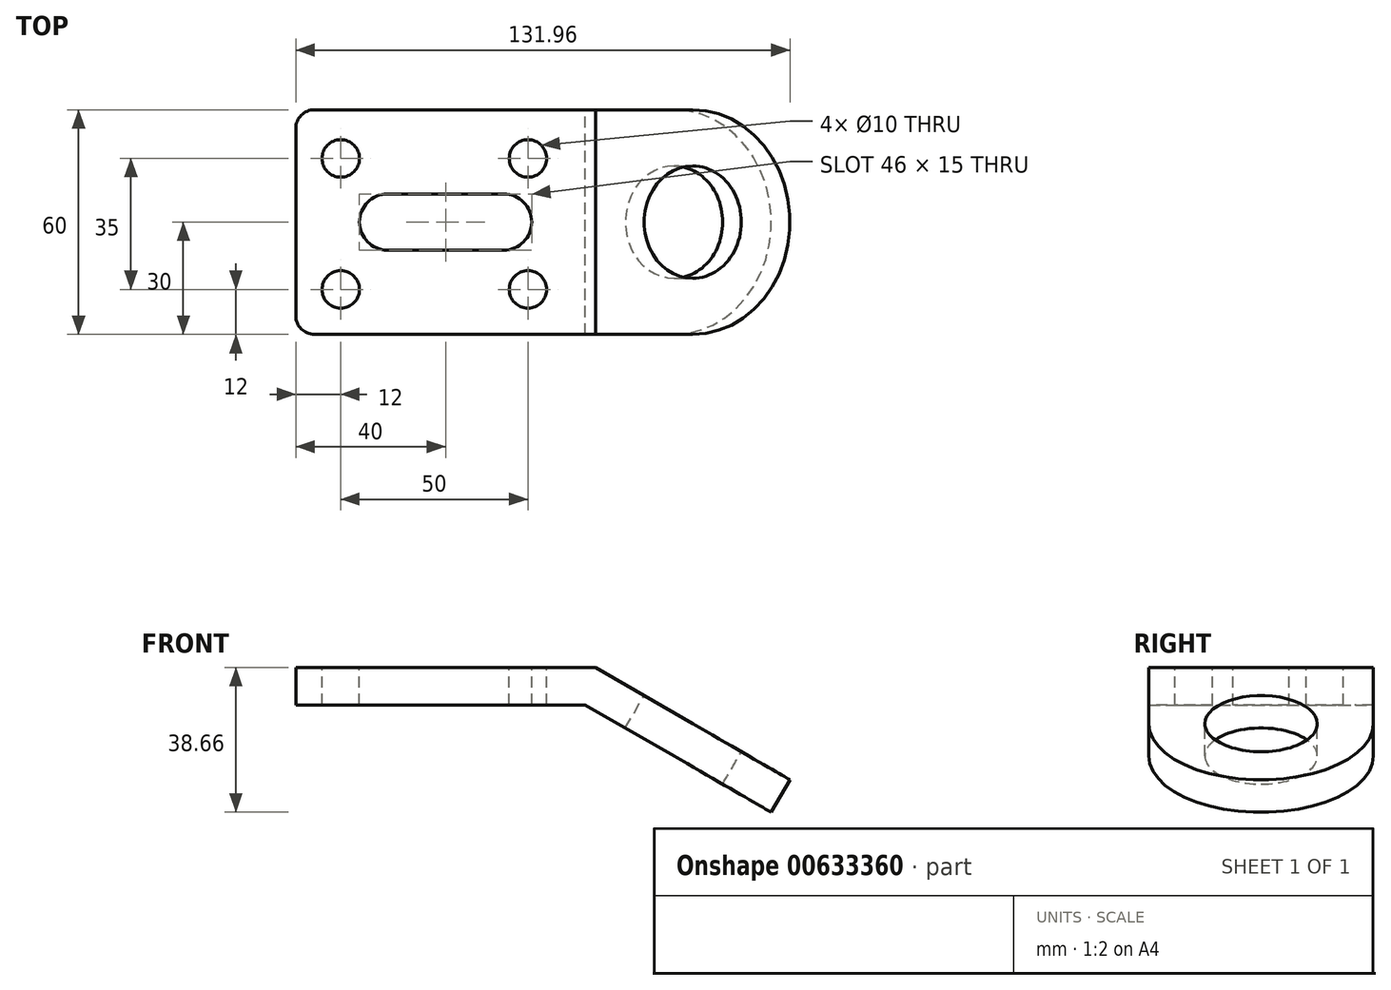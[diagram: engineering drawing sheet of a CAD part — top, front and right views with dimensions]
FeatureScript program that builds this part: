
annotation { "Feature Type Name" : "Feature", "Feature Type Description" : "" }
export const myFeature = defineFeature(function(context is Context, id is Id, definition is map)
    precondition{}
    {
        {
            var Q0;
            Q0=qCreatedBy(makeId("Front.planeOp"),FACE);
            var sketch = newSketch(context, id + "F0", { "sketchPlane" : qUnion([Q0])});
            skLineSegment(sketch, "E0", {"start": v(0, 0) * mm, "end": v(80, 0) * mm});
            skLineSegment(sketch, "E1", {"start": v(80, 0) * mm, "end": v(131.96, -30) * mm});
            skLineSegment(sketch, "E2.0", {"start": v(77.32, -10) * mm, "end": v(126.96, -38.66) * mm});
            skLineSegment(sketch, "E2.1", {"start": v(0, -10) * mm, "end": v(77.32, -10) * mm});
            skLineSegment(sketch, "E3", {"start": v(0, 0) * mm, "end": v(0, -10) * mm});
            skLineSegment(sketch, "E4", {"start": v(131.96, -30) * mm, "end": v(126.96, -38.66) * mm});
            skSolve(sketch);
        }
        {
            var Q0;
            Q0 = qSketchRegion(id + "F0", true);
            extrude(context, id + "F1", {"entities" : qUnion([Q0]), "depth" : 60 * mm, "offsetDistance" : 25 * mm});
        }
        {
            var Q0;
            Q0=makeQuery(id+"F1.opExtrude","CAP_EDGE",EDGE,{"disambiguationData":[OSD([sQuery(id+"F0.wireOp",EDGE,"E4")])],"isStart":false});
            var Q1;
            Q1=makeQuery(id+"F1.opExtrude","CAP_EDGE",EDGE,{"disambiguationData":[OSD([sQuery(id+"F0.wireOp",EDGE,"E4")])],"isStart":true});
            fillet(context, id + "F2", {"entities" : qUnion([Q0, Q1]), "radius" : 30 * mm, "tangentPropagation" : true, "allowEdgeOverflow" : false});
        }
        {
            var Q0;
            Q0=makeQuery(id+"F1.opExtrude","SWEPT_FACE",FACE,{"disambiguationData":[OSD([sQuery(id+"F0.wireOp",EDGE,"E1")])]});
            var sketch = newSketch(context, id + "F3", { "sketchPlane" : qUnion([Q0])});
            skCircle(sketch, "E5", {"center": v(99.28, -30) * mm, "radius": 15 * mm});
            skSolve(sketch);
        }
        {
            var Q0;
            Q0 = qSketchRegion(id + "F3", true);
            extrude(context, id + "F4", {"entities" : qUnion([Q0]), "operationType" : NewBodyOperationType.REMOVE, "endBound" : BoundingType.UP_TO_NEXT, "oppositeDirection" : true, "depth" : 25 * mm, "offsetDistance" : 25 * mm});
        }
        {
            var Q0;
            Q0=makeQuery(id+"F1.opExtrude","SWEPT_FACE",FACE,{"disambiguationData":[OSD([sQuery(id+"F0.wireOp",EDGE,"E0")])]});
            var sketch = newSketch(context, id + "F5", { "sketchPlane" : qUnion([Q0])});
            skCircle(sketch, "E6", {"center": v(12, -48) * mm, "radius": 5 * mm});
            skCircle(sketch, "E7.0.1.0", {"center": v(12, -13) * mm, "radius": 5 * mm});
            skCircle(sketch, "E7.1.0.0", {"center": v(62, -48) * mm, "radius": 5 * mm});
            skCircle(sketch, "E7.1.1.0", {"center": v(62, -13) * mm, "radius": 5 * mm});
            skLineSegment(sketch, "E7.direction1", {"start": v(12, -48) * mm, "end": v(62, -48) * mm, "construction": true});
            skLineSegment(sketch, "E7.direction2", {"start": v(12, -48) * mm, "end": v(12, -13) * mm, "construction": true});
            skSolve(sketch);
        }
        {
            var Q0;
            Q0 = qSketchRegion(id + "F5", true);
            extrude(context, id + "F6", {"entities" : qUnion([Q0]), "operationType" : NewBodyOperationType.REMOVE, "endBound" : BoundingType.UP_TO_NEXT, "oppositeDirection" : true, "depth" : 25 * mm, "offsetDistance" : 25 * mm});
        }
        {
            var Q0;
            Q0=makeQuery(id+"F1.opExtrude","SWEPT_FACE",FACE,{"disambiguationData":[OSD([sQuery(id+"F0.wireOp",EDGE,"E0")])]});
            var sketch = newSketch(context, id + "F7", { "sketchPlane" : qUnion([Q0])});
            skLineSegment(sketch, "E8.bottom", {"start": v(55.5, -37.5) * mm, "end": v(24.5, -37.5) * mm});
            skLineSegment(sketch, "E8.top", {"start": v(55.5, -22.5) * mm, "end": v(24.5, -22.5) * mm});
            skLineSegment(sketch, "E8.left", {"start": v(63, -30) * mm, "end": v(63, -30) * mm});
            skLineSegment(sketch, "E8.right", {"start": v(17, -30) * mm, "end": v(17, -30) * mm});
            skPoint(sketch, "E8.middle", {"position": v(40, -30) * mm});
            skPoint(sketch, "E8.middle.positionSnap0", {"position": v(0, -30) * mm});
            skPoint(sketch, "E8.middle.positionSnap1", {"position": v(40, 0) * mm});
            skPoint(sketch, "E8.centerSnap0", {"position": v(0, -30) * mm});
            skPoint(sketch, "E8.centerSnap1", {"position": v(40, 0) * mm});
            skPoint(sketch, "E9.visualSharp", {"position": v(17, -37.5) * mm});
            skArc(sketch, "E9.filletArc", {"start": v(17, -30) * mm, "mid": v(19.2, -35.3) * mm, "end": v(24.5, -37.5) * mm});
            skPoint(sketch, "E10.visualSharp", {"position": v(17, -22.5) * mm});
            skArc(sketch, "E10.filletArc", {"start": v(24.5, -22.5) * mm, "mid": v(19.2, -24.7) * mm, "end": v(17, -30) * mm});
            skPoint(sketch, "E11.visualSharp", {"position": v(63, -22.5) * mm});
            skArc(sketch, "E11.filletArc", {"start": v(63, -30) * mm, "mid": v(60.8, -24.7) * mm, "end": v(55.5, -22.5) * mm});
            skPoint(sketch, "E12.visualSharp", {"position": v(63, -37.5) * mm});
            skArc(sketch, "E12.filletArc", {"start": v(55.5, -37.5) * mm, "mid": v(60.8, -35.3) * mm, "end": v(63, -30) * mm});
            skSolve(sketch);
        }
        {
            var Q0;
            Q0 = qSketchRegion(id + "F7", true);
            extrude(context, id + "F8", {"entities" : qUnion([Q0]), "operationType" : NewBodyOperationType.REMOVE, "endBound" : BoundingType.UP_TO_NEXT, "oppositeDirection" : true, "depth" : 25 * mm, "offsetDistance" : 25 * mm});
        }
        {
            var Q0;
            Q0=makeQuery(id+"F1.opExtrude","CAP_EDGE",EDGE,{"disambiguationData":[OSD([sQuery(id+"F0.wireOp",EDGE,"E3")])],"isStart":false});
            var Q1;
            Q1=makeQuery(id+"F1.opExtrude","CAP_EDGE",EDGE,{"disambiguationData":[OSD([sQuery(id+"F0.wireOp",EDGE,"E3")])],"isStart":true});
            fillet(context, id + "F9", {"entities" : qUnion([Q0, Q1]), "radius" : 5 * mm, "tangentPropagation" : true, "allowEdgeOverflow" : false});
        }
    });
